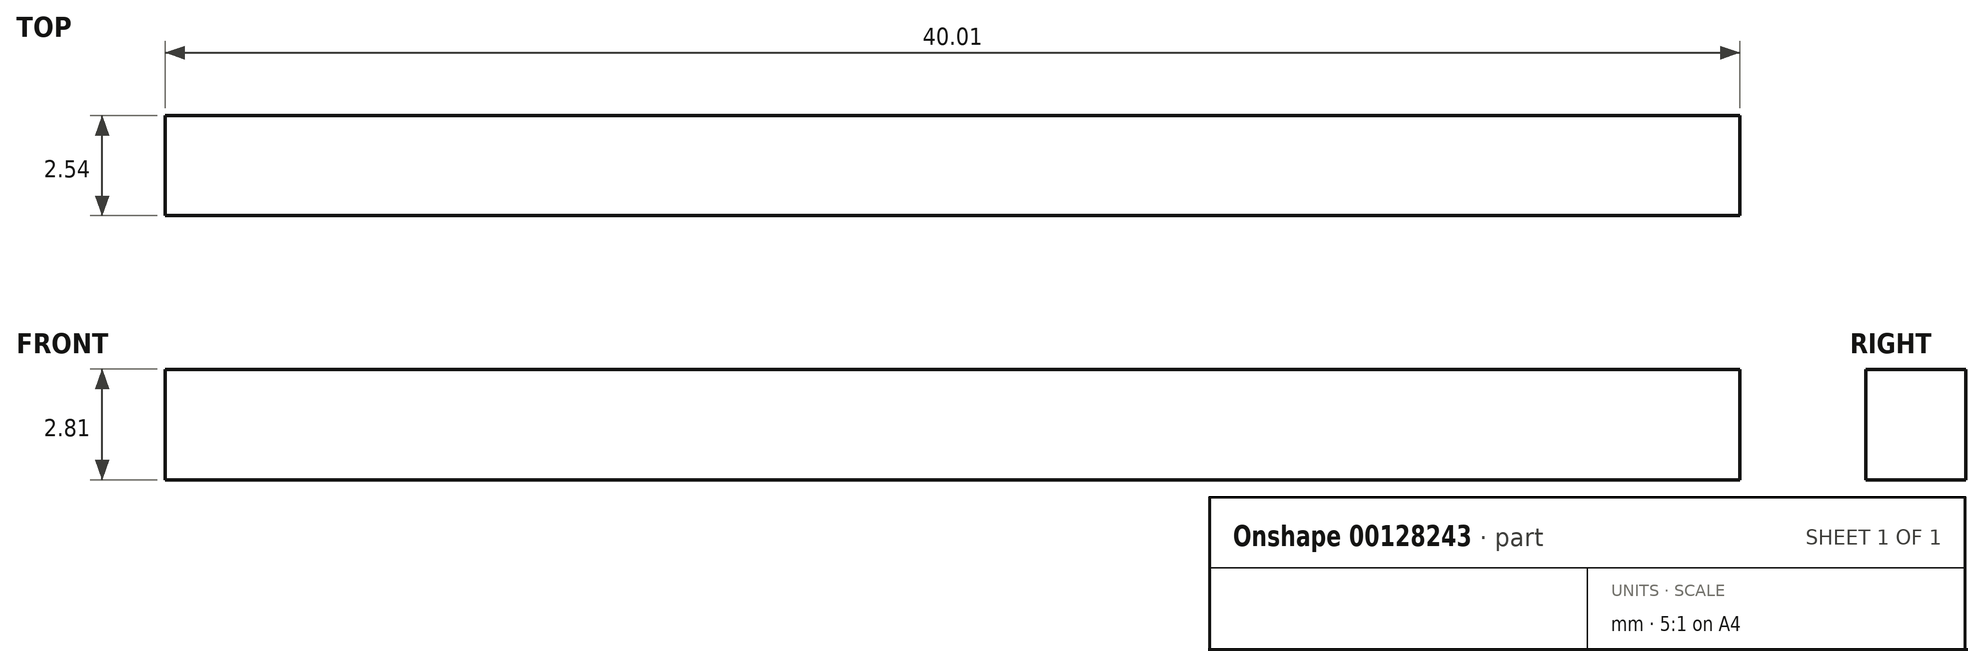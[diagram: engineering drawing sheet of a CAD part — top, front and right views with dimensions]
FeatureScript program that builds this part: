
annotation { "Feature Type Name" : "Feature", "Feature Type Description" : "" }
export const myFeature = defineFeature(function(context is Context, id is Id, definition is map)
    precondition{}
    {
        {
            var Q0;
            Q0=qCreatedBy(makeId("Front.planeOp"),FACE);
            var sketch = newSketch(context, id + "F0", { "sketchPlane" : qUnion([Q0])});
            skLineSegment(sketch, "E0.bottom", {"start": v(-66.89, 12.56) * mm, "end": v(-26.88, 12.56) * mm});
            skLineSegment(sketch, "E0.top", {"start": v(-66.89, 9.75) * mm, "end": v(-26.88, 9.75) * mm});
            skLineSegment(sketch, "E0.left", {"start": v(-66.89, 12.56) * mm, "end": v(-66.89, 9.75) * mm});
            skLineSegment(sketch, "E0.right", {"start": v(-26.88, 12.56) * mm, "end": v(-26.88, 9.75) * mm});
            skSolve(sketch);
        }
        {
            var Q0;
            Q0 = qSketchRegion(id + "F0", true);
            extrude(context, id + "F1", {"entities" : qUnion([Q0]), "depth" : 2.54 * mm});
        }
    });
